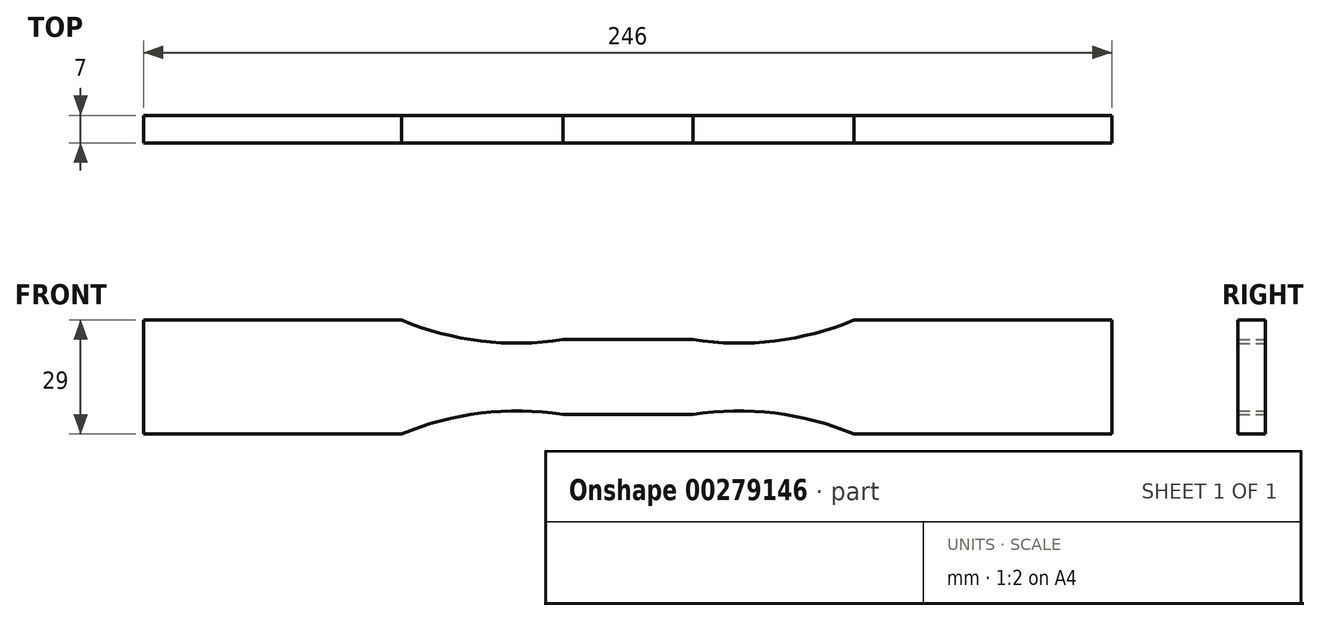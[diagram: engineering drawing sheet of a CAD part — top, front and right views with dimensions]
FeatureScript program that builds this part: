
annotation { "Feature Type Name" : "Feature", "Feature Type Description" : "" }
export const myFeature = defineFeature(function(context is Context, id is Id, definition is map)
    precondition{}
    {
        {
            var Q0;
            Q0=qCreatedBy(makeId("Front.planeOp"),FACE);
            var sketch = newSketch(context, id + "F0", { "sketchPlane" : qUnion([Q0])});
            skLineSegment(sketch, "E0", {"start": v(0, 9.5) * mm, "end": v(16.5, 9.5) * mm});
            skArc(sketch, "E1", {"start": v(16.5, 9.5) * mm, "mid": v(37.35, 9.16) * mm, "end": v(57.5, 14.5) * mm});
            skLineSegment(sketch, "E2", {"start": v(57.5, 14.5) * mm, "end": v(123, 14.5) * mm});
            skLineSegment(sketch, "E3.MirrorCS", {"start": v(57.5, -14.5) * mm, "end": v(123, -14.5) * mm});
            skLineSegment(sketch, "E4.MirrorCS", {"start": v(0, -9.5) * mm, "end": v(16.5, -9.5) * mm});
            skArc(sketch, "E5.MirrorCS", {"start": v(16.5, -9.5) * mm, "mid": v(37.35, -9.16) * mm, "end": v(57.5, -14.5) * mm});
            skArc(sketch, "E6.MirrorCS", {"start": v(-16.5, -9.5) * mm, "mid": v(-37.35, -9.16) * mm, "end": v(-57.5, -14.5) * mm});
            skLineSegment(sketch, "E7.MirrorCS", {"start": v(0, 9.5) * mm, "end": v(-16.5, 9.5) * mm});
            skArc(sketch, "E8.MirrorCS", {"start": v(-16.5, 9.5) * mm, "mid": v(-37.35, 9.16) * mm, "end": v(-57.5, 14.5) * mm});
            skLineSegment(sketch, "E9.MirrorCS", {"start": v(-57.5, 14.5) * mm, "end": v(-123, 14.5) * mm});
            skLineSegment(sketch, "E10.MirrorCS", {"start": v(-57.5, -14.5) * mm, "end": v(-123, -14.5) * mm});
            skLineSegment(sketch, "E11.MirrorCS", {"start": v(0, -9.5) * mm, "end": v(-16.5, -9.5) * mm});
            skLineSegment(sketch, "E12", {"start": v(123, 14.5) * mm, "end": v(123, -14.5) * mm});
            skLineSegment(sketch, "E13", {"start": v(-123, 14.5) * mm, "end": v(-123, -14.5) * mm});
            skSolve(sketch);
        }
        {
            var Q0;
            Q0=makeQuery(id+"F0.imprint","IMPRINT",FACE,{"disambiguationData":[TD([[makeQuery(id+"F0.imprint","IMPRINT",EDGE,{"derivedFrom":sQuery(id+"F0.wireOp",EDGE,"E0")}),-1.0]])]});
            extrude(context, id + "F1", {"entities" : qUnion([Q0]), "endBound" : BoundingType.SYMMETRIC, "depth" : 7 * mm});
        }
    });
